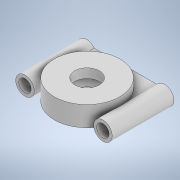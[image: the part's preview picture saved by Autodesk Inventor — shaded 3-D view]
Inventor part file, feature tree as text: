
AUTODESK INVENTOR PART (.ipt)
format: ipt  version: 2021 (Build 250183000, 183)  size: 156,672 bytes
history: native  units: mm
features: sketch x5, extrude x4, projected_geometry x1
ambient origin geometry x8: Origin, YZ Plane, XZ Plane, XY Plane, X Axis, Y Axis, Z Axis, Center Point
bodies: Solid1 (feature_tree)
feature tree (10):
  extrude  "Extrusion1"  Depth=7.0mm TaperAngle=0.0deg
  extrude  "Extrusion2"  Depth=6.0mm TaperAngle=0.0deg
  sketch  "Sketch3"  dims[d8=115.0mm d9=0.0mm d10=4.0mm]
  extrude  "Extrusion3"  Depth=4.0mm
  extrude  "Extrusion4"  Depth=12.0mm
  sketch  "Sketch1"  dims[d0=22.5mm d3=7.0mm d4=0.0mm]
  sketch  "Sketch2"  dims[d5=16.0mm d6=6.0mm d7=0.0mm]
  sketch  "Sketch4"  dims[d11=8.0mm d12=12.0mm]
  projected_geometry  "Projected Loop1"
  sketch  "Sketch5"  dims[d13=4.0mm d14=12.0mm d15=40.0mm d16=0.0mm]
